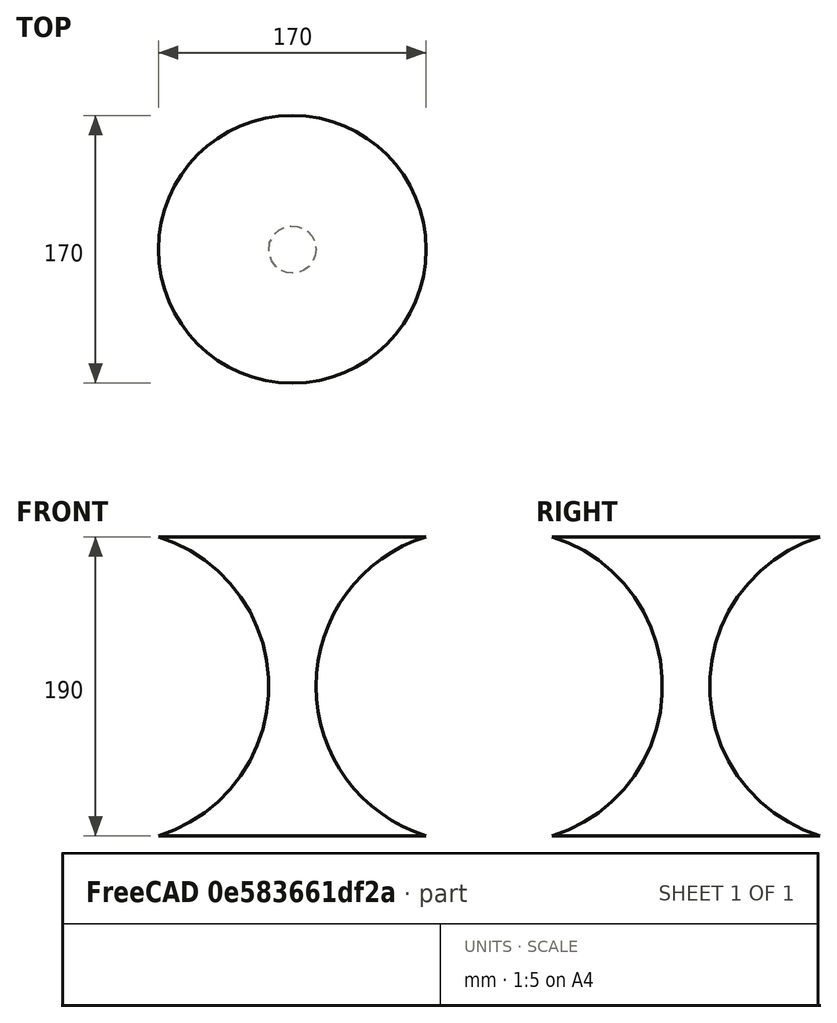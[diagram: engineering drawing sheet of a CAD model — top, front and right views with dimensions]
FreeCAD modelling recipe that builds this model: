
FCSTD DOCUMENT  (FreeCAD 2022.111R30764 (Git))
Label: speaker stand
License: All rights reserved
LicenseURL: http://en.wikipedia.org/wiki/All_rights_reserved
objects: Sketcher::SketchObject×3, PartDesign::Plane×1, PartDesign::Revolution×1, PartDesign::Body×1
note: 8 computed .brp shape members not serialized (recipe doc carries the construction recipe); baked Part::Feature solids carry a one-line shape summary decoded from their .brp

FEATURE [Sketcher::SketchObject] Sketch
  FullyConstrained = true
  MapMode = 5
  Support = -> [XY_Plane]
  TreeRank = 11
  sketch-geometry (1):
    g0: Circle CenterX=0 CenterY=0 CenterZ=0 NormalX=0 NormalY=0 NormalZ=1 AngleXU=0 Radius=85
  constraints (2):
    c: Coincident(g0,g-1)
    c: Diameter(g0) = 170
FEATURE [PartDesign::Plane] DatumPlane
  AttachmentOffset = pos=(0,0,190) rot=(0,0,1;0rad)
  Length = 169.724
  MapMode = 2
  MinimumLength = 10
  MinimumWidth = 10
  Placement = pos=(0,0,190) rot=(0,0,1;0rad)
  ResizeMode = 0
  Support = -> [Sketch]
  TreeRank = 12
  Width = 169.862
FEATURE [Sketcher::SketchObject] Sketch001
  FullyConstrained = true
  MapMode = 5
  Placement = pos=(0,0,190) rot=(0,0,1;0rad)
  Support = -> [DatumPlane]
  TreeRank = 13
  sketch-geometry (1):
    g0: Circle CenterX=0 CenterY=0 CenterZ=0 NormalX=0 NormalY=0 NormalZ=1 AngleXU=0 Radius=85
  constraints (2):
    c: Coincident(g0,g-1)
    c: Diameter(g0) = 170
FEATURE [Sketcher::SketchObject] Sketch002
  ExternalGeometry = -> [Sketch,Sketch001]
  FullyConstrained = true
  MapMode = 5
  Placement = pos=(0,0,0) rot=(1,0,0;1.5708rad)
  Support = -> [XZ_Plane]
  TreeRank = 14
  sketch-geometry (6):
    g0: ArcOfCircle CenterX=114.464 CenterY=95 CenterZ=0 NormalX=0 NormalY=0 NormalZ=1 AngleXU=0 Radius=99.4643 StartAngle=1.87154 EndAngle=4.41165
    g1: LineSegment StartX=85 StartY=190 StartZ=0 EndX=0 EndY=190 EndZ=0
    g2: LineSegment StartX=0 StartY=190 StartZ=0 EndX=0 EndY=0 EndZ=0
    g3: LineSegment StartX=0 StartY=0 StartZ=0 EndX=85 EndY=-1.42e-14 EndZ=0
    g4: GeomPoint [constr] X=15 Y=95 Z=0
    g5: GeomPoint [constr] X=0 Y=95 Z=0
  constraints (14):
    c: Coincident(g0,g-4)
    c: Coincident(g0,g-3)
    c: Coincident(g1,g0)
    c: PointOnObject(g1,g-4)
    c: Coincident(g2,g1)
    c: Coincident(g2,g-1)
    c: Vertical(g2)
    c: Coincident(g3,g2)
    c: Coincident(g3,g0)
    c: PointOnObject(g4,g0)
    c: Horizontal(g4,g0)
    c: PointOnObject(g5,g2)
    c: Horizontal(g5,g4)
    c: DistanceX(g5,g4) = 15
FEATURE [PartDesign::Revolution] Revolution
  AddSubType = 0
  Angle = 360
  Axis = (0,2e-16,1)
  Base = (0,0,0)
  ClaimChildren = false
  Fit = 0
  FitJoin = 0
  InnerFit = 0
  InnerFitJoin = 0
  Linearize = true
  NewSolid = false
  Placement = pos=(0,0,0) rot=(1,0,0;1.5708rad)
  Profile = -> Sketch002
  ReferenceAxis = -> Sketch002 [V_Axis]
  Suppress = false
  TreeRank = 15
  _ProfileBasedVersion = 1
FEATURE [PartDesign::Body] Body
  AutoGroupSolids = false
  ExportMode = 0
  Group = -> [Sketch,DatumPlane,Sketch001,Sketch002,Revolution]
  Origin = -> Origin
  Tip = -> Revolution
  TreeRank = 10
  _ExportChildren = -> [Sketch,DatumPlane,Sketch001,Revolution]
  _GroupVersion = 1
